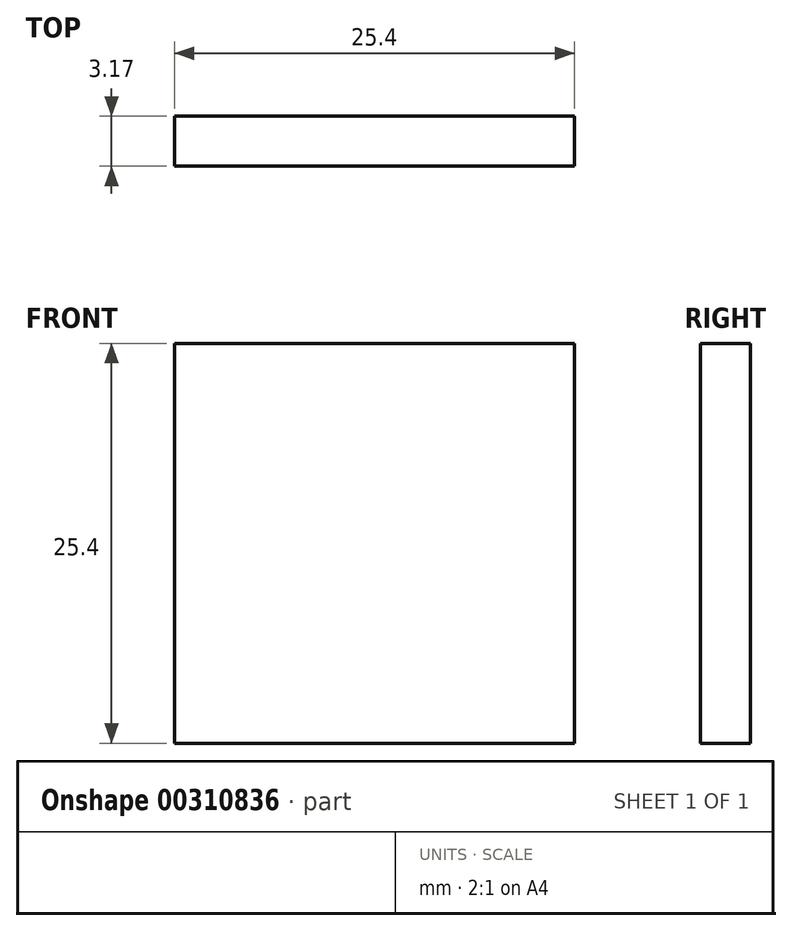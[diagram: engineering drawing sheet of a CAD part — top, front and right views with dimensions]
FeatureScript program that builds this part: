
annotation { "Feature Type Name" : "Feature", "Feature Type Description" : "" }
export const myFeature = defineFeature(function(context is Context, id is Id, definition is map)
    precondition{}
    {
        {
            var Q0;
            Q0=qCreatedBy(makeId("Front.planeOp"),FACE);
            var sketch = newSketch(context, id + "F0", { "sketchPlane" : qUnion([Q0])});
            skLineSegment(sketch, "E0.bottom", {"start": v(3.96, 29.86) * mm, "end": v(29.36, 29.86) * mm});
            skLineSegment(sketch, "E0.top", {"start": v(3.96, 4.46) * mm, "end": v(29.36, 4.46) * mm});
            skLineSegment(sketch, "E0.left", {"start": v(3.96, 29.86) * mm, "end": v(3.96, 4.46) * mm});
            skLineSegment(sketch, "E0.right", {"start": v(29.36, 29.86) * mm, "end": v(29.36, 4.46) * mm});
            skSolve(sketch);
        }
        {
            var Q0;
            Q0=makeQuery(id+"F0.imprint","IMPRINT",FACE,{"disambiguationData":[TD([[makeQuery(id+"F0.imprint","IMPRINT",EDGE,{"derivedFrom":sQuery(id+"F0.wireOp",EDGE,"E0.bottom")}),-1.0]])]});
            extrude(context, id + "F1", {"entities" : qUnion([Q0]), "depth" : 3.17 * mm});
        }
    });
